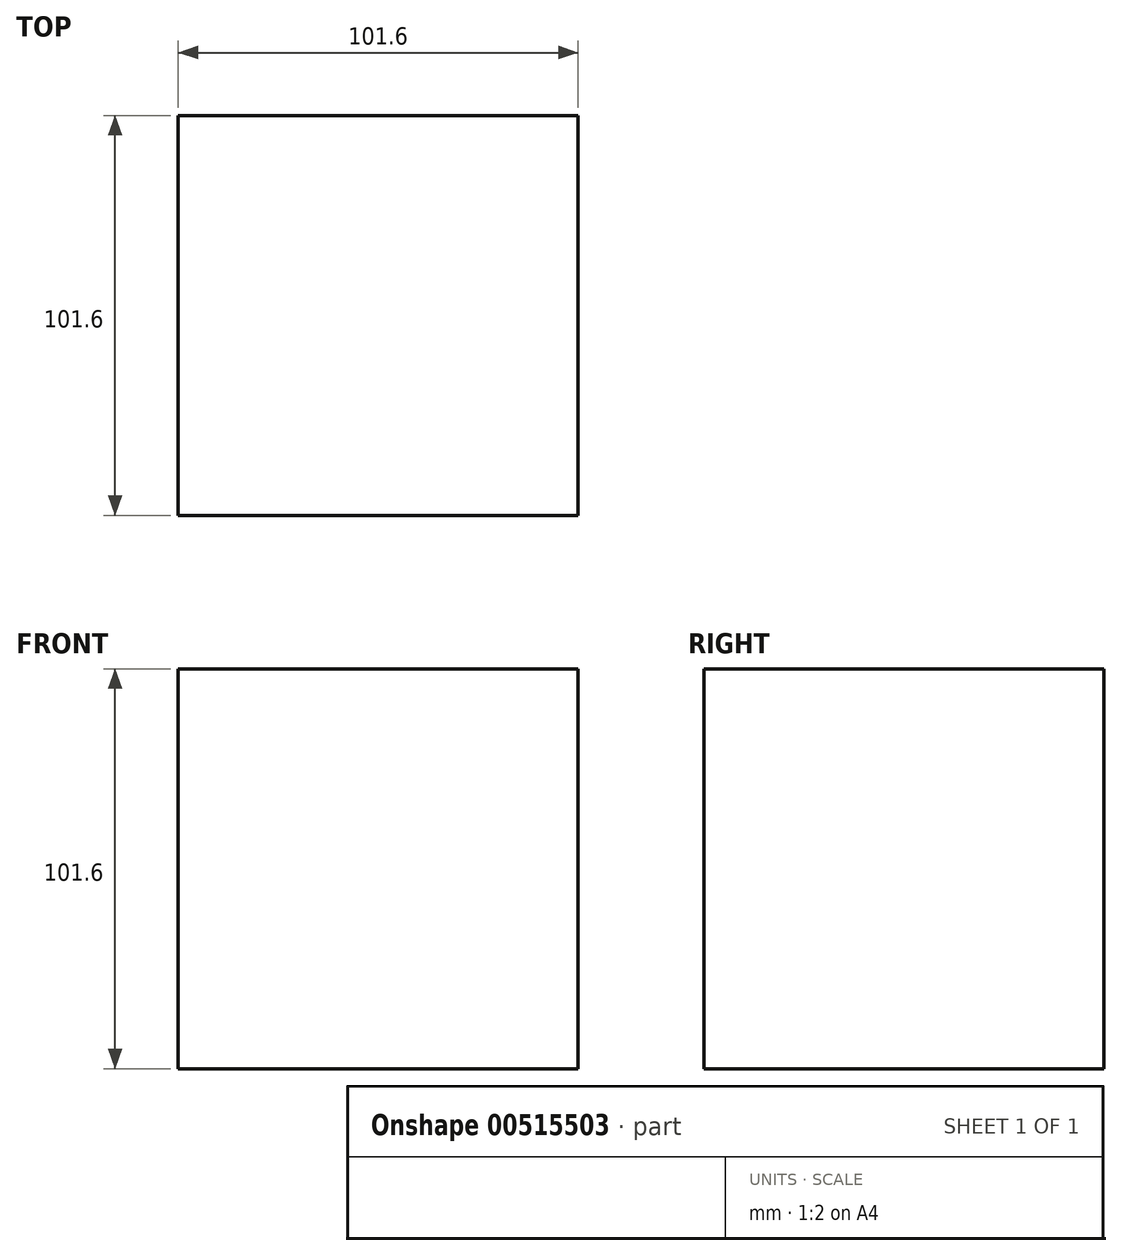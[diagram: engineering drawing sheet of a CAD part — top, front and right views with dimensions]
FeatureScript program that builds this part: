
annotation { "Feature Type Name" : "Feature", "Feature Type Description" : "" }
export const myFeature = defineFeature(function(context is Context, id is Id, definition is map)
    precondition{}
    {
        {
            var Q0;
            Q0=qCreatedBy(makeId("Front.planeOp"),FACE);
            var sketch = newSketch(context, id + "F0", { "sketchPlane" : qUnion([Q0])});
            skLineSegment(sketch, "E0.bottom", {"start": v(-52.8, 50.37) * mm, "end": v(48.8, 50.37) * mm});
            skLineSegment(sketch, "E0.top", {"start": v(-52.8, -51.23) * mm, "end": v(48.8, -51.23) * mm});
            skLineSegment(sketch, "E0.left", {"start": v(-52.8, 50.37) * mm, "end": v(-52.8, -51.23) * mm});
            skLineSegment(sketch, "E0.right", {"start": v(48.8, 50.37) * mm, "end": v(48.8, -51.23) * mm});
            skSolve(sketch);
        }
        {
            var Q0;
            Q0 = qSketchRegion(id + "F0", true);
            extrude(context, id + "F1", {"entities" : qUnion([Q0]), "depth" : 101.6 * mm, "offsetDistance" : 25.4 * mm});
        }
        {
            var Q0;
            Q0=qCreatedBy(makeId("Front.planeOp"),FACE);
            var sketch = newSketch(context, id + "F2", { "sketchPlane" : qUnion([Q0])});
            skCircle(sketch, "E1", {"center": v(0, 0) * mm, "radius": 7.43 * mm});
            skSolve(sketch);
        }
        {
            var Q0;
            Q0 = qSketchRegion(id + "F2", true);
            extrude(context, id + "F3", {"entities" : qUnion([Q0]), "operationType" : NewBodyOperationType.ADD, "depth" : 25.4 * mm, "offsetDistance" : 25.4 * mm});
        }
    });
